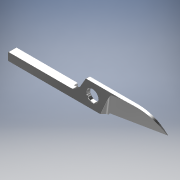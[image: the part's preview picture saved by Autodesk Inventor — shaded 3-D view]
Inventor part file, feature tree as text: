
AUTODESK INVENTOR PART (.ipt)
format: ipt  version: 2019 (Build 230136000, 136)  size: 227,840 bytes
history: native  units: mm (DEFAULTED — no unit token found)
features: sketch x8, fillet x5, extrude x4, plane x3, sweep x1, chamfer x1
ambient origin geometry x8: Origin, YZ Plane, XZ Plane, XY Plane, X Axis, Y Axis, Z Axis, Center Point
bodies: Solid1 (feature_tree)
feature tree (22):
  extrude  "Extrusion1"  Depth=42.0mm
  fillet  "Fillet1"  Radius=21.5mm
  extrude  "Extrusion2"  Depth=3.0mm
  sketch  "Sketch4"  dims[d6=11.0mm d7=2.0mm d8=20.5mm d9=2.0mm d10=0.0mm d11=120.0deg]
  sketch  "Sketch5"  dims[d12=4.0mm d13=3.0mm]
  plane  "Work Plane3"
  extrude  "Extrusion3"  Depth=2.0mm
  fillet  "Fillet2"  Radius=20.5mm
  fillet  "Fillet4"  Radius=2.0mm
  fillet  "Fillet5"  [1 undecoded]
  plane  "Work Plane4"
  sketch  "Sketch7"  dims[d19=75.0deg]
  plane  "Work Plane5"
  sweep  "Sweep1"
  extrude  "Extrusion4"  Depth=3.0mm
  fillet  "Fillet6"  Radius=15.0mm
  chamfer  "Chamfer1"  Distance=0.1mm
  sketch  "Sketch1"  dims[d0=2.9mm d1=42.0mm d3=21.5mm]
  sketch  "Sketch3"  dims[d4=6.0mm d5=3.0mm]
  sketch  "Sketch6"  dims[d15=2.0mm d16=0.0mm d17=3.0mm d18=15.0mm]
  sketch  "Sketch8"  dims[d20=0.5mm]
  sketch  "Sketch9"  dims[d21=23.5mm d24=0.1mm d25=0.4mm d26=5.0mm d27=15.5mm d28=6.5mm d29=15.5mm d30=2.0mm d31=0.0mm d32=45.0deg d33=0.25mm d35=1.6mm d36=1.0mm d37=0.25mm d38=-0.3mm d39=0.0mm d40=10.0mm d41=0.0mm d42=0.2mm d43=0.1mm d44=0.1mm d45=45.0deg d46=0.0mm]
note: 1 required parameter value undecoded (feature->parameter linkage not recoverable at this tier; creation-order binding heuristic only, values carry confidence <= 0.55)
